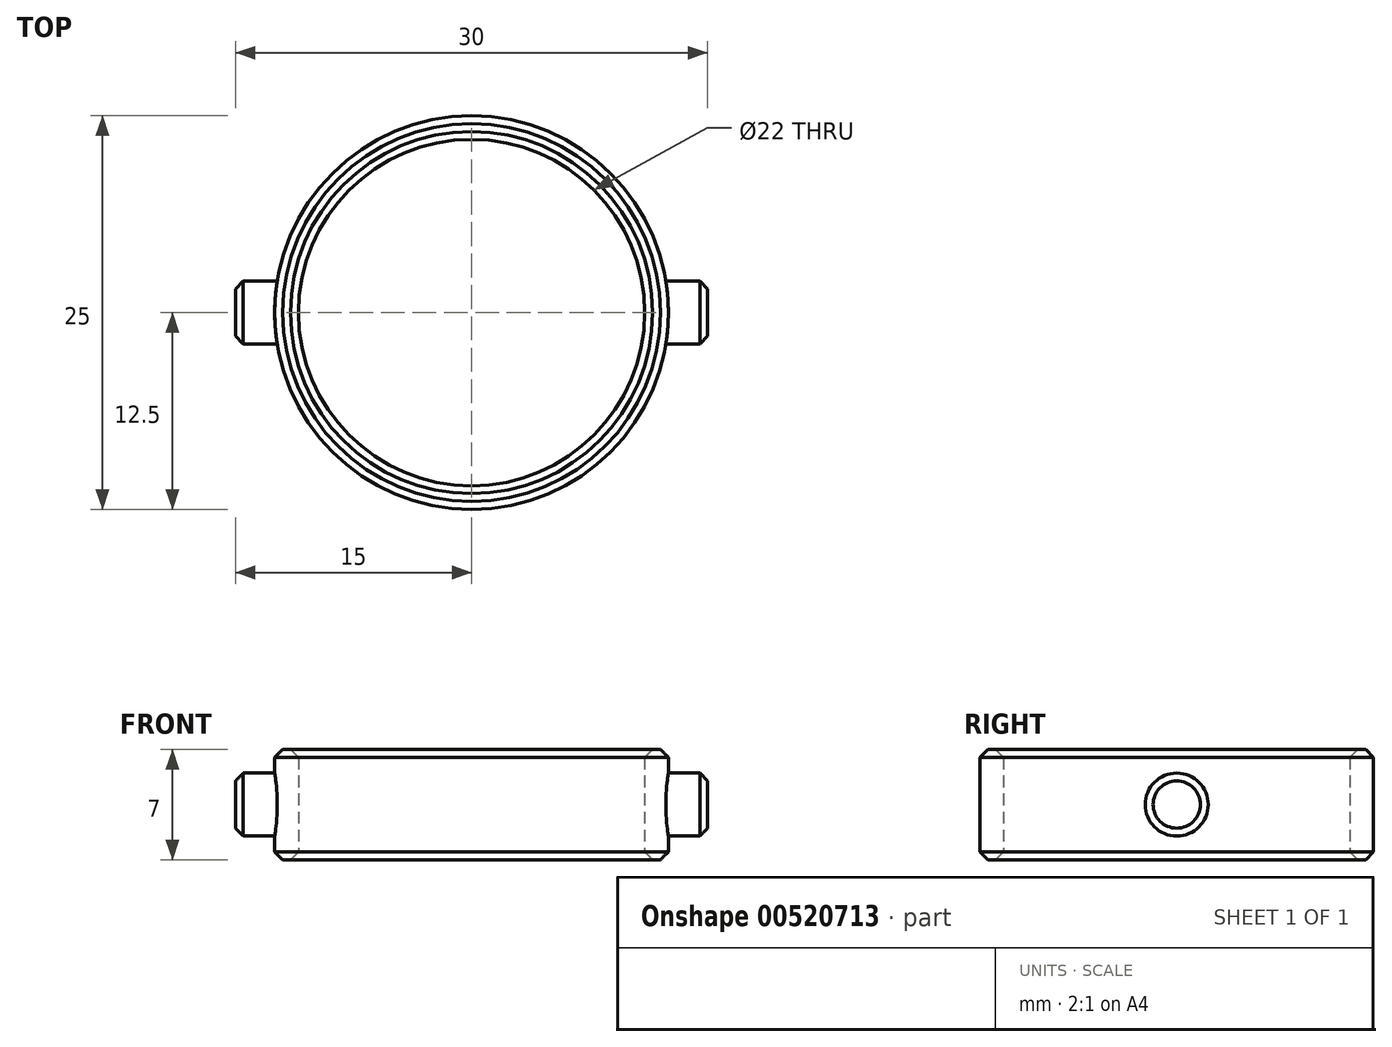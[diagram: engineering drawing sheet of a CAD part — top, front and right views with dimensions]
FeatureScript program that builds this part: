
annotation { "Feature Type Name" : "Feature", "Feature Type Description" : "" }
export const myFeature = defineFeature(function(context is Context, id is Id, definition is map)
    precondition{}
    {
        {
            var Q0;
            Q0=qCreatedBy(makeId("Top.planeOp"),FACE);
            var sketch = newSketch(context, id + "F0", { "sketchPlane" : qUnion([Q0])});
            skCircle(sketch, "E0", {"center": v(0, 0) * mm, "radius": 11 * mm});
            skCircle(sketch, "E1", {"center": v(0, 0) * mm, "radius": 12.5 * mm});
            skSolve(sketch);
        }
        {
            var Q0;
            Q0=makeQuery(id+"F0.imprint","IMPRINT",FACE,{"disambiguationData":[TD([[makeQuery(id+"F0.imprint","IMPRINT",EDGE,{"derivedFrom":sQuery(id+"F0.wireOp",EDGE,"E0")}),-1.0]])]});
            extrude(context, id + "F1", {"entities" : qUnion([Q0]), "depth" : 7 * mm});
        }
        {
            var Q0;
            Q0=makeQuery(id+"F1.opExtrude","CAP_EDGE",EDGE,{"disambiguationData":[OSD([sQuery(id+"F0.wireOp",EDGE,"E0")])],"isStart":false});
            var Q1;
            Q1=makeQuery(id+"F1.opExtrude","CAP_EDGE",EDGE,{"disambiguationData":[OSD([sQuery(id+"F0.wireOp",EDGE,"E1")])],"isStart":false});
            var Q2;
            Q2=makeQuery(id+"F1.opExtrude","CAP_EDGE",EDGE,{"disambiguationData":[OSD([sQuery(id+"F0.wireOp",EDGE,"E1")])],"isStart":true});
            var Q3;
            Q3=makeQuery(id+"F1.opExtrude","CAP_EDGE",EDGE,{"disambiguationData":[OSD([sQuery(id+"F0.wireOp",EDGE,"E0")])],"isStart":true});
            chamfer(context, id + "F2", {"entities" : qUnion([Q0, Q1, Q2, Q3]), "width" : .5 * mm, "tangentPropagation" : true});
        }
        {
            var Q0;
            Q0=qCreatedBy(makeId("Right.planeOp"),FACE);
            cPlane(context, id + "F3", {"entities" : qUnion([Q0]), "cplaneType" : CPlaneType.OFFSET, "offset" : 11 * mm, "width" : 150 * mm, "height" : 150 * mm});
        }
        {
            var Q0;
            Q0=qCreatedBy(id+"F3.planeOp",FACE);
            var sketch = newSketch(context, id + "F4", { "sketchPlane" : qUnion([Q0])});
            skCircle(sketch, "E2", {"center": v(0, 3.5) * mm, "radius": 2 * mm});
            skLineSegment(sketch, "E3", {"start": v(0, 3.5) * mm, "end": v(0, 7) * mm, "construction": true});
            skLineSegment(sketch, "E4", {"start": v(0, 3.5) * mm, "end": v(0, 0) * mm, "construction": true});
            skSolve(sketch);
        }
        {
            var Q0;
            Q0=qSketchRegion(id+"F4",true);
            var Q1;
            Q1=sQuery(id+"F4.wireOp",EDGE,"E2");
            extrude(context, id + "F5", {"entities" : qUnion([Q0]), "operationType" : NewBodyOperationType.ADD, "surfaceEntities" : qUnion([Q1]), "depth" : 4 * mm});
        }
        {
            var Q0;
            Q0=makeQuery(id+"F1.opExtrude","SWEPT_BODY",BODY,{"disambiguationData":[OSD([sQuery(id+"F0.wireOp",EDGE,"E0"),sQuery(id+"F0.wireOp",EDGE,"E1")])]});
            var Q1;
            Q1=qCreatedBy(makeId("Right.planeOp"),FACE);
            mirror(context, id + "F6", {"operationType" : NewBodyOperationType.ADD, "entities" : qUnion([Q0]), "mirrorPlane" : qUnion([Q1])});
        }
        {
            var Q0;
            Q0=makeQuery(id+"F5.opExtrude","CAP_EDGE",EDGE,{"disambiguationData":[OSD([sQuery(id+"F4.wireOp",EDGE,"E2")])],"isStart":false});
            var Q1;
            Q1=makeQuery(id+"F6.opPattern","COPY",EDGE,{"derivedFrom":makeQuery(id+"F5.opExtrude","CAP_EDGE",EDGE,{"disambiguationData":[OSD([sQuery(id+"F4.wireOp",EDGE,"E2")])],"isStart":false}),"instanceName":"1"});
            chamfer(context, id + "F7", {"entities" : qUnion([Q0, Q1]), "width" : .5 * mm, "tangentPropagation" : true});
        }
    });
